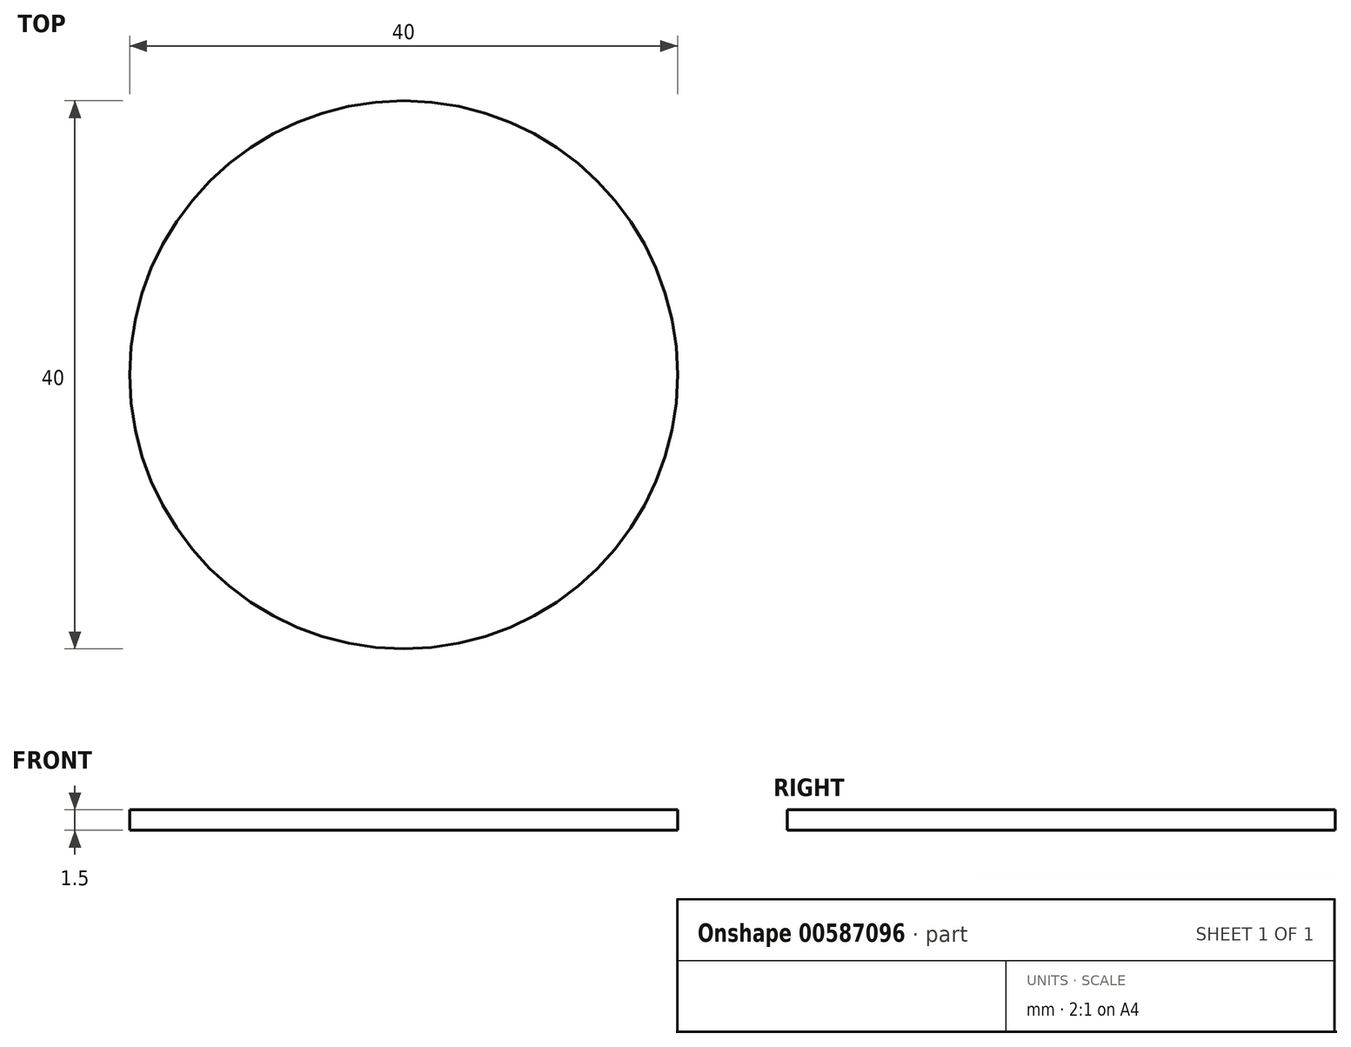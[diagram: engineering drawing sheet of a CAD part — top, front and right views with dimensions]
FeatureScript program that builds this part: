
annotation { "Feature Type Name" : "Feature", "Feature Type Description" : "" }
export const myFeature = defineFeature(function(context is Context, id is Id, definition is map)
    precondition{}
    {
        {
            var Q0;
            Q0=qCreatedBy(makeId("Top.planeOp"),FACE);
            var sketch = newSketch(context, id + "F0", { "sketchPlane" : qUnion([Q0])});
            skCircle(sketch, "E0", {"center": v(0, 0) * mm, "radius": 20 * mm});
            skSolve(sketch);
        }
        {
            var Q0;
            Q0 = qSketchRegion(id + "F0", true);
            extrude(context, id + "F1", {"entities" : qUnion([Q0]), "depth" : 1.5 * mm, "offsetDistance" : 25 * mm});
        }
    });
